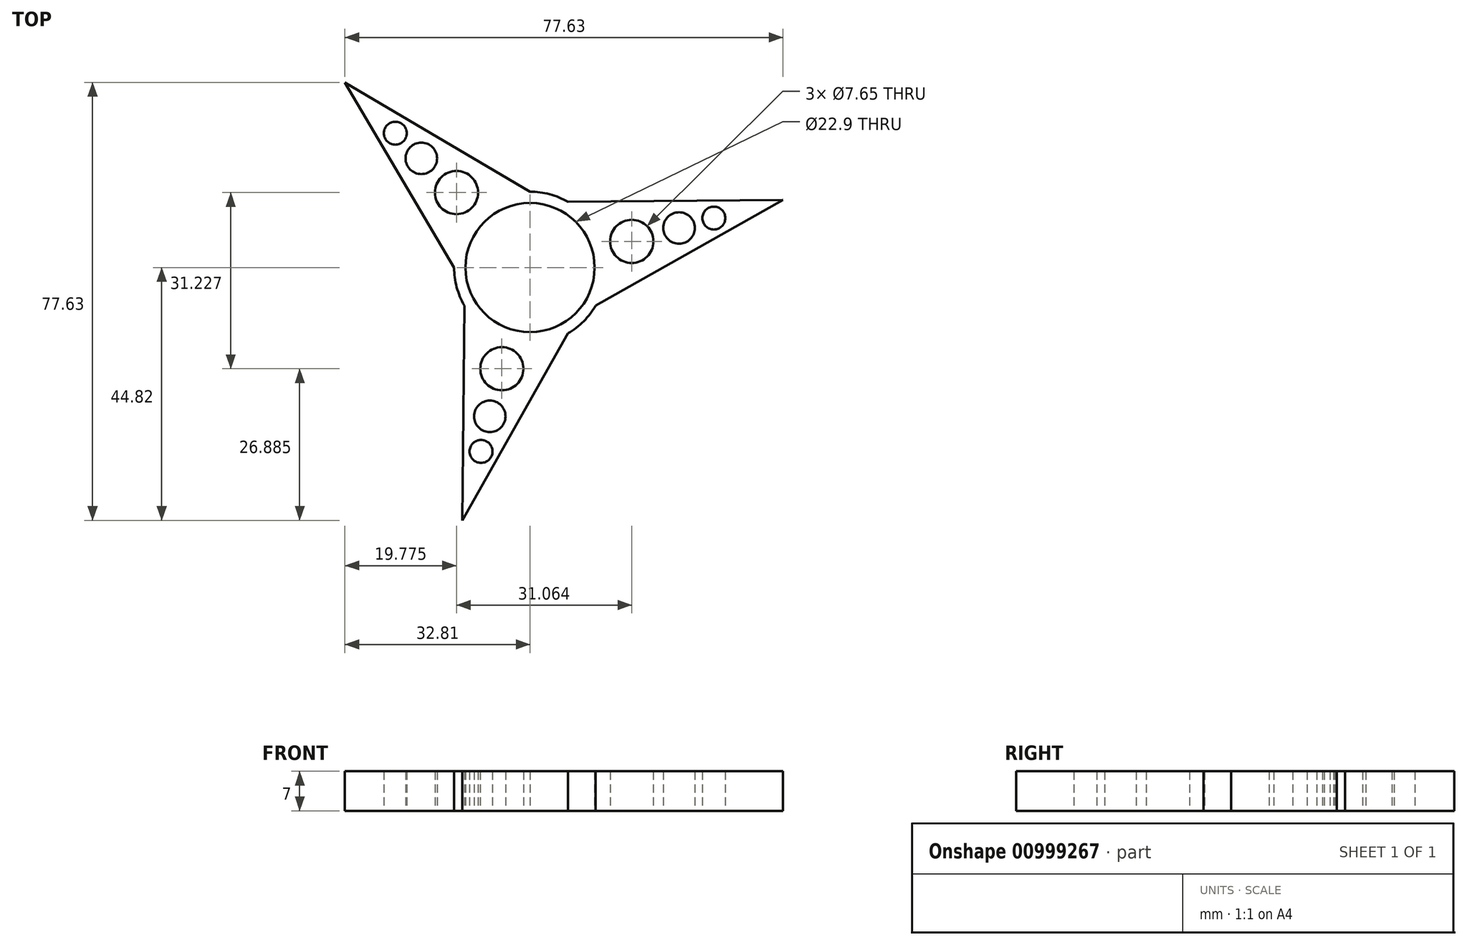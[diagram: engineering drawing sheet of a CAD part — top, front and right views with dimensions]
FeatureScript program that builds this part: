
annotation { "Feature Type Name" : "Feature", "Feature Type Description" : "" }
export const myFeature = defineFeature(function(context is Context, id is Id, definition is map)
    precondition{}
    {
        {
            var Q0;
            Q0=qCreatedBy(makeId("Top.planeOp"),FACE);
            var sketch = newSketch(context, id + "F0", { "sketchPlane" : qUnion([Q0])});
            skCircle(sketch, "E0", {"center": v(0, 0) * mm, "radius": 11.45 * mm});
            skCircle(sketch, "E1", {"center": v(0, 0) * mm, "radius": 13.45 * mm});
            skLineSegment(sketch, "E2", {"start": v(-13.45, 0) * mm, "end": v(-32.81, 32.81) * mm});
            skLineSegment(sketch, "E3", {"start": v(-32.81, 32.81) * mm, "end": v(0, 13.45) * mm});
            skCircle(sketch, "E4", {"center": v(-13.04, 13.3) * mm, "radius": 3.83 * mm});
            skCircle(sketch, "E5", {"center": v(-19.28, 19.37) * mm, "radius": 2.8 * mm});
            skCircle(sketch, "E6", {"center": v(-23.88, 23.83) * mm, "radius": 2.03 * mm});
            skLineSegment(sketch, "E7.1.0", {"start": v(-12.01, -44.82) * mm, "end": v(-11.65, -6.72) * mm});
            skCircle(sketch, "E7.1.1", {"center": v(-8.7, -32.6) * mm, "radius": 2.03 * mm});
            skLineSegment(sketch, "E7.1.2", {"start": v(6.72, -11.65) * mm, "end": v(-12.01, -44.82) * mm});
            skCircle(sketch, "E7.1.3", {"center": v(-7.14, -26.38) * mm, "radius": 2.8 * mm});
            skCircle(sketch, "E7.1.4", {"center": v(-5, -17.93) * mm, "radius": 3.83 * mm});
            skLineSegment(sketch, "E7.2.0", {"start": v(44.82, 12.01) * mm, "end": v(11.65, -6.73) * mm});
            skCircle(sketch, "E7.2.1", {"center": v(32.58, 8.77) * mm, "radius": 2.03 * mm});
            skLineSegment(sketch, "E7.2.2", {"start": v(6.73, 11.65) * mm, "end": v(44.82, 12.01) * mm});
            skCircle(sketch, "E7.2.3", {"center": v(26.41, 7) * mm, "radius": 2.8 * mm});
            skCircle(sketch, "E7.2.4", {"center": v(18.03, 4.64) * mm, "radius": 3.83 * mm});
            skSolve(sketch);
        }
        {
            var Q0;
            Q0 = qSketchRegion(id + "F0", true);
            extrude(context, id + "F1", {"entities" : qUnion([Q0]), "depth" : 7 * mm, "offsetDistance" : 25.4 * mm});
        }
    });
